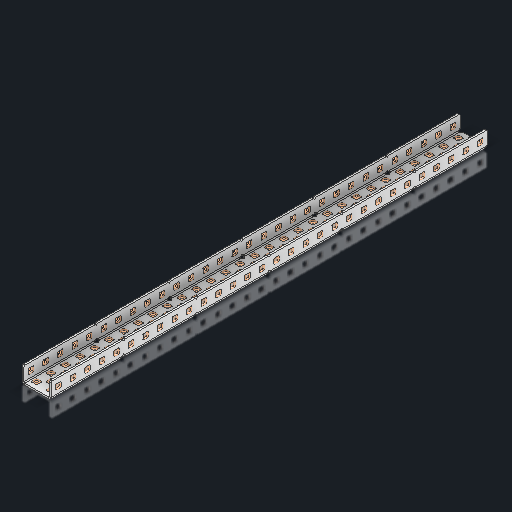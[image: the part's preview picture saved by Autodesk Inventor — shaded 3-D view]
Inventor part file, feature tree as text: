
AUTODESK INVENTOR PART (.ipt)
format: ipt  version: 2023.2 (Build 272271030, 271C)  size: 1,822,720 bytes
history: native  units: in
note: dims shown in document units (in); Inventor stores cm internally (conversion verified against a paired STEP export)
features: other x157, extrude x148, sheet_metal_op x11, sketch x10, pattern_linear x2, mirror x1, chamfer x1
ambient origin geometry x8: Origin, YZ Plane, XZ Plane, XY Plane, X Axis, Y Axis, Z Axis, Center Point
bodies: Solid1 (feature_tree), Body (feature_tree)
feature tree (330):
  sheet_metal_op  "Flanges"
  other  "Flange Pattern Plane"
  other  "Flange Pattern Sketch"
  sheet_metal_op  "Flange Pattern"
  sheet_metal_op  "Body Pattern"
  pattern_linear  "Center Pattern"  Spacing1=0.0625in  [1 undecoded]
  other  "Arc Length"
  mirror  "Notch Mirror"
  pattern_linear  "Notch Pattern"  Spacing1=0.182in  [1 undecoded]
  chamfer  "End Chamfer"
  extrude  "Half Cut"  Depth=0.02in
  sketch  "Sketch1"  dims[d0=1.0in]
  other  "Plate1"
  sketch  "Sketch2"  dims[d1=15.0in]
  other  "Plate2"
  sheet_metal_op  "Bend1"
  sheet_metal_op  "Corner1"
  sketch  "Sketch3"  dims[d2=0.0625in]
  sketch  "Sketch7"  dims[d3=0.0625in]
  other  "Srf1"
  other  "Srf2"
  sketch  "Sketch8"  dims[d4=0.0312in]
  sketch  "Sketch9"  dims[d5=0.125in]
  other  "Srf91"
  sheet_metal_op  "Body Pattern Sketch"
  other  "Srf92"
  sketch  "Sketch13"  dims[d6=0.0625in]
  sketch  "Sketch14"  dims[d7=0.5in d8=90.0deg d9=0.0312in]
  sketch  "Sketch15"  dims[d10=0.25in]
  sketch  "Sketch16"  dims[d11=0.0625in d12=0.0625in d16=0.182in d17=0.02in d18=0.0625in d19=0.0in d20=0.25in d21=0.25in d38=11.811in d40=0.5in d41=0.7874in d43=1.0in d46=0.172in d47=1.0in d48=0.0in d49=0.182in d50=0.02in d51=0.25in d52=0.25in d53=0.0625in d54=0.0in d55=0.172in d56=1.0in d57=0.0in d58=0.25in d60=11.811in d62=0.5in d63=0.7874in d65=0.5in d85=0.1473in d86=0.1782in d88=0.04in d89=0.0625in d90=0.0in d91=0.04in d92=0.0491in d95=2.5in d96=0.04in d97=0.25in d98=45.0deg d99=0.25in d100=0.5in d101=0.0in d102=2.497in d106=0.182in d107=0.02in d108=0.5in d109=0.5in d110=0.0625in d111=0.0in d112=0.172in d113=0.5in d114=0.0in d117=0.5in d118=0.5in d119=0.5in]
  other  "Srf786"
  other  "Srf823"
  other  "Srf824"
  other  "Srf825"
  other  "Srf826"
  other  "Srf827"
  other  "Srf828"
  other  "Srf829"
  other  "Srf856"
  other  "Srf857"
  other  "Srf858"
  other  "Srf859"
  other  "Srf860"
  other  "Srf861"
  other  "Srf862"
  other  "Srf889"
  other  "Srf890"
  other  "Srf891"
  other  "Srf892"
  other  "Srf893"
  other  "Srf894"
  other  "Srf895"
  other  "Srf896"
  other  "Srf922"
  other  "Srf923"
  other  "Srf924"
  other  "Srf925"
  other  "Srf926"
  other  "Srf959"
  other  "Srf960"
  other  "Srf961"
  other  "Srf962"
  other  "Srf963"
  other  "Srf996"
  other  "Srf997"
  other  "Srf998"
  other  "Srf999"
  other  "Srf1000"
  other  "Srf1143"
  other  "Srf1144"
  other  "Srf1145"
  other  "Srf1146"
  other  "Srf1147"
  other  "Srf1148"
  other  "Srf1149"
  other  "Srf1150"
  other  "Srf1151"
  other  "Srf1152"
  other  "Srf1153"
  other  "Srf1154"
  other  "Srf1155"
  other  "Srf1156"
  other  "Srf1157"
  other  "Srf1158"
  other  "Srf1159"
  other  "Srf1160"
  other  "Srf1161"
  other  "Srf1162"
  other  "Srf1163"
  other  "Srf1164"
  other  "Srf1165"
  other  "Srf1166"
  other  "Srf1167"
  other  "Srf1168"
  other  "Srf1169"
  other  "Srf1170"
  other  "Srf1171"
  other  "Srf1172"
  other  "Srf1173"
  other  "Srf1174"
  other  "Srf1175"
  other  "Srf1176"
  other  "Srf1177"
  other  "Srf1178"
  other  "Srf1179"
  other  "Srf1180"
  other  "Srf1181"
  other  "Srf1182"
  other  "Srf1183"
  other  "Srf1184"
  other  "Srf1185"
  other  "Srf1186"
  other  "Srf1187"
  other  "Srf1188"
  other  "Srf1199"
  other  "Srf1200"
  other  "Srf1201"
  other  "Srf1202"
  other  "Srf1203"
  other  "Srf1204"
  other  "Srf1205"
  other  "Srf1206"
  other  "Srf1207"
  other  "Srf1208"
  other  "Srf1209"
  other  "Srf1210"
  other  "Srf1211"
  other  "Srf1212"
  other  "Srf1213"
  other  "Srf1214"
  other  "Srf1215"
  other  "Srf1216"
  other  "Srf1217"
  other  "Srf1218"
  other  "Srf1219"
  other  "Srf1220"
  other  "Srf1221"
  other  "Srf1222"
  other  "Srf1223"
  other  "Srf1224"
  other  "Srf1225"
  other  "Srf1226"
  other  "Srf1227"
  other  "Srf1228"
  other  "Srf1229"
  other  "Srf1230"
  other  "Srf1231"
  other  "Srf1232"
  other  "Srf1233"
  other  "Srf1234"
  other  "Srf1235"
  other  "Srf1236"
  other  "Srf1237"
  other  "Srf1238"
  other  "Srf1239"
  other  "Srf1240"
  other  "Srf1241"
  other  "Srf1242"
  other  "Srf1243"
  other  "Srf1244"
  other  "Srf1255"
  other  "Srf1256"
  other  "Srf1257"
  other  "Srf1258"
  other  "Srf1259"
  other  "Srf1260"
  other  "Srf1261"
  other  "Srf1262"
  other  "Srf1263"
  other  "Srf1264"
  other  "Srf1265"
  other  "Srf1266"
  other  "Srf1267"
  other  "Srf1268"
  other  "Srf1269"
  other  "Srf1270"
  sheet_metal_op  "Flange Stamp"
  sheet_metal_op  "Flange Circle"
  sheet_metal_op  "Body Stamp"
  sheet_metal_op  "Body Circle"
  other  "Center Stamp"
  other  "Center Circle"
  sheet_metal_op  "Notch"
  extrude  "ExtrusionSrf2"  Depth=0.0625in
  extrude  "ExtrusionSrf92"  TaperAngle=0.0deg  [1 undecoded]
  extrude  "ExtrusionSrf823"  Depth=0.5in
  extrude  "ExtrusionSrf824"  Depth=0.5in
  extrude  "ExtrusionSrf825"  Depth=0.5in
  extrude  "ExtrusionSrf826"  Depth=0.5in
  extrude  "ExtrusionSrf827"  Depth=1.0in TaperAngle=0.0deg
  extrude  "ExtrusionSrf828"  Depth=0.5in
  extrude  "ExtrusionSrf829"  Depth=0.02in
  extrude  "ExtrusionSrf856"  Depth=0.5in
  extrude  "ExtrusionSrf857"  Depth=0.5in
  extrude  "ExtrusionSrf858"  Depth=0.0625in
  extrude  "ExtrusionSrf859"  TaperAngle=0.0deg  [1 undecoded]
  extrude  "ExtrusionSrf860"  Depth=0.5in
  extrude  "ExtrusionSrf861"  Depth=1.0in TaperAngle=0.0deg
  extrude  "ExtrusionSrf862"  Depth=0.5in
  extrude  "ExtrusionSrf889"  Depth=0.5in
  extrude  "ExtrusionSrf890"  Depth=0.5in
  extrude  "ExtrusionSrf891"  Depth=0.5in
  extrude  "ExtrusionSrf892"  Depth=0.5in
  extrude  "ExtrusionSrf893"  Depth=0.5in
  extrude  "ExtrusionSrf894"  Depth=0.0625in
  extrude  "ExtrusionSrf895"  TaperAngle=0.0deg  [1 undecoded]
  extrude  "ExtrusionSrf896"  Depth=0.5in
  extrude  "ExtrusionSrf922"  Depth=0.5in
  extrude  "ExtrusionSrf923"  Depth=2.5in
  extrude  "ExtrusionSrf924"  Depth=0.5in TaperAngle=45.0deg
  extrude  "ExtrusionSrf925"  Depth=0.5in
  extrude  "ExtrusionSrf926"  Depth=0.5in TaperAngle=0.0deg
  extrude  "ExtrusionSrf959"  Depth=0.5in
  extrude  "ExtrusionSrf960"  Depth=0.5in
  extrude  "ExtrusionSrf961"  Depth=0.02in
  extrude  "ExtrusionSrf962"  Depth=0.5in
  extrude  "ExtrusionSrf963"  Depth=0.5in
  extrude  "ExtrusionSrf996"  Depth=0.0625in
  extrude  "ExtrusionSrf997"  TaperAngle=0.0deg  [1 undecoded]
  extrude  "ExtrusionSrf998"  Depth=0.5in
  extrude  "ExtrusionSrf999"  Depth=0.5in TaperAngle=0.0deg
  extrude  "ExtrusionSrf1000"  Depth=0.5in
  extrude  "ExtrusionSrf1143"  Depth=0.5in
  extrude  "ExtrusionSrf1144"  Depth=0.5in
  extrude  "ExtrusionSrf1145"  [1 undecoded]
  extrude  "ExtrusionSrf1146"  [1 undecoded]
  extrude  "ExtrusionSrf1147"  [1 undecoded]
  extrude  "ExtrusionSrf1148"  [1 undecoded]
  extrude  "ExtrusionSrf1149"  [1 undecoded]
  extrude  "ExtrusionSrf1150"  [1 undecoded]
  extrude  "ExtrusionSrf1151"  [1 undecoded]
  extrude  "ExtrusionSrf1152"  [1 undecoded]
  extrude  "ExtrusionSrf1153"  [1 undecoded]
  extrude  "ExtrusionSrf1154"  [1 undecoded]
  extrude  "ExtrusionSrf1155"  [1 undecoded]
  extrude  "ExtrusionSrf1156"  [1 undecoded]
  extrude  "ExtrusionSrf1157"  [1 undecoded]
  extrude  "ExtrusionSrf1158"  [1 undecoded]
  extrude  "ExtrusionSrf1159"  [1 undecoded]
  extrude  "ExtrusionSrf1160"  [1 undecoded]
  extrude  "ExtrusionSrf1161"  [1 undecoded]
  extrude  "ExtrusionSrf1162"  [1 undecoded]
  extrude  "ExtrusionSrf1163"  [1 undecoded]
  extrude  "ExtrusionSrf1164"  [1 undecoded]
  extrude  "ExtrusionSrf1165"  [1 undecoded]
  extrude  "ExtrusionSrf1166"  [1 undecoded]
  extrude  "ExtrusionSrf1167"  [1 undecoded]
  extrude  "ExtrusionSrf1168"  [1 undecoded]
  extrude  "ExtrusionSrf1169"  [1 undecoded]
  extrude  "ExtrusionSrf1170"  [1 undecoded]
  extrude  "ExtrusionSrf1171"  [1 undecoded]
  extrude  "ExtrusionSrf1172"  [1 undecoded]
  extrude  "ExtrusionSrf1173"  [1 undecoded]
  extrude  "ExtrusionSrf1174"  [1 undecoded]
  extrude  "ExtrusionSrf1175"  [1 undecoded]
  extrude  "ExtrusionSrf1176"  [1 undecoded]
  extrude  "ExtrusionSrf1177"  [1 undecoded]
  extrude  "ExtrusionSrf1178"  [1 undecoded]
  extrude  "ExtrusionSrf1179"  [1 undecoded]
  extrude  "ExtrusionSrf1180"  [1 undecoded]
  extrude  "ExtrusionSrf1181"  [1 undecoded]
  extrude  "ExtrusionSrf1182"  [1 undecoded]
  extrude  "ExtrusionSrf1183"  [1 undecoded]
  extrude  "ExtrusionSrf1184"  [1 undecoded]
  extrude  "ExtrusionSrf1185"  [1 undecoded]
  extrude  "ExtrusionSrf1186"  [1 undecoded]
  extrude  "ExtrusionSrf1187"  [1 undecoded]
  extrude  "ExtrusionSrf1188"  [1 undecoded]
  extrude  "ExtrusionSrf1199"  [1 undecoded]
  extrude  "ExtrusionSrf1200"  [1 undecoded]
  extrude  "ExtrusionSrf1201"  [1 undecoded]
  extrude  "ExtrusionSrf1202"  [1 undecoded]
  extrude  "ExtrusionSrf1203"  [1 undecoded]
  extrude  "ExtrusionSrf1204"  [1 undecoded]
  extrude  "ExtrusionSrf1205"  [1 undecoded]
  extrude  "ExtrusionSrf1206"  [1 undecoded]
  extrude  "ExtrusionSrf1207"  [1 undecoded]
  extrude  "ExtrusionSrf1208"  [1 undecoded]
  extrude  "ExtrusionSrf1209"  [1 undecoded]
  extrude  "ExtrusionSrf1210"  [1 undecoded]
  extrude  "ExtrusionSrf1211"  [1 undecoded]
  extrude  "ExtrusionSrf1212"  [1 undecoded]
  extrude  "ExtrusionSrf1213"  [1 undecoded]
  extrude  "ExtrusionSrf1214"  [1 undecoded]
  extrude  "ExtrusionSrf1215"  [1 undecoded]
  extrude  "ExtrusionSrf1216"  [1 undecoded]
  extrude  "ExtrusionSrf1217"  [1 undecoded]
  extrude  "ExtrusionSrf1218"  [1 undecoded]
  extrude  "ExtrusionSrf1219"  [1 undecoded]
  extrude  "ExtrusionSrf1220"  [1 undecoded]
  extrude  "ExtrusionSrf1221"  [1 undecoded]
  extrude  "ExtrusionSrf1222"  [1 undecoded]
  extrude  "ExtrusionSrf1223"  [1 undecoded]
  extrude  "ExtrusionSrf1224"  [1 undecoded]
  extrude  "ExtrusionSrf1225"  [1 undecoded]
  extrude  "ExtrusionSrf1226"  [1 undecoded]
  extrude  "ExtrusionSrf1227"  [1 undecoded]
  extrude  "ExtrusionSrf1228"  [1 undecoded]
  extrude  "ExtrusionSrf1229"  [1 undecoded]
  extrude  "ExtrusionSrf1230"  [1 undecoded]
  extrude  "ExtrusionSrf1231"  [1 undecoded]
  extrude  "ExtrusionSrf1232"  [1 undecoded]
  extrude  "ExtrusionSrf1233"  [1 undecoded]
  extrude  "ExtrusionSrf1234"  [1 undecoded]
  extrude  "ExtrusionSrf1235"  [1 undecoded]
  extrude  "ExtrusionSrf1236"  [1 undecoded]
  extrude  "ExtrusionSrf1237"  [1 undecoded]
  extrude  "ExtrusionSrf1238"  [1 undecoded]
  extrude  "ExtrusionSrf1239"  [1 undecoded]
  extrude  "ExtrusionSrf1240"  [1 undecoded]
  extrude  "ExtrusionSrf1241"  [1 undecoded]
  extrude  "ExtrusionSrf1242"  [1 undecoded]
  extrude  "ExtrusionSrf1243"  [1 undecoded]
  extrude  "ExtrusionSrf1244"  [1 undecoded]
  extrude  "ExtrusionSrf1255"  [1 undecoded]
  extrude  "ExtrusionSrf1256"  [1 undecoded]
  extrude  "ExtrusionSrf1257"  [1 undecoded]
  extrude  "ExtrusionSrf1258"  [1 undecoded]
  extrude  "ExtrusionSrf1259"  [1 undecoded]
  extrude  "ExtrusionSrf1260"  [1 undecoded]
  extrude  "ExtrusionSrf1261"  [1 undecoded]
  extrude  "ExtrusionSrf1262"  [1 undecoded]
  extrude  "ExtrusionSrf1263"  [1 undecoded]
  extrude  "ExtrusionSrf1264"  [1 undecoded]
  extrude  "ExtrusionSrf1265"  [1 undecoded]
  extrude  "ExtrusionSrf1266"  [1 undecoded]
  extrude  "ExtrusionSrf1267"  [1 undecoded]
  extrude  "ExtrusionSrf1268"  [1 undecoded]
  extrude  "ExtrusionSrf1269"  [1 undecoded]
  extrude  "ExtrusionSrf1270"  [1 undecoded]
note: 112 required parameter values undecoded (feature->parameter linkage not recoverable at this tier; creation-order binding heuristic only, values carry confidence <= 0.55)
